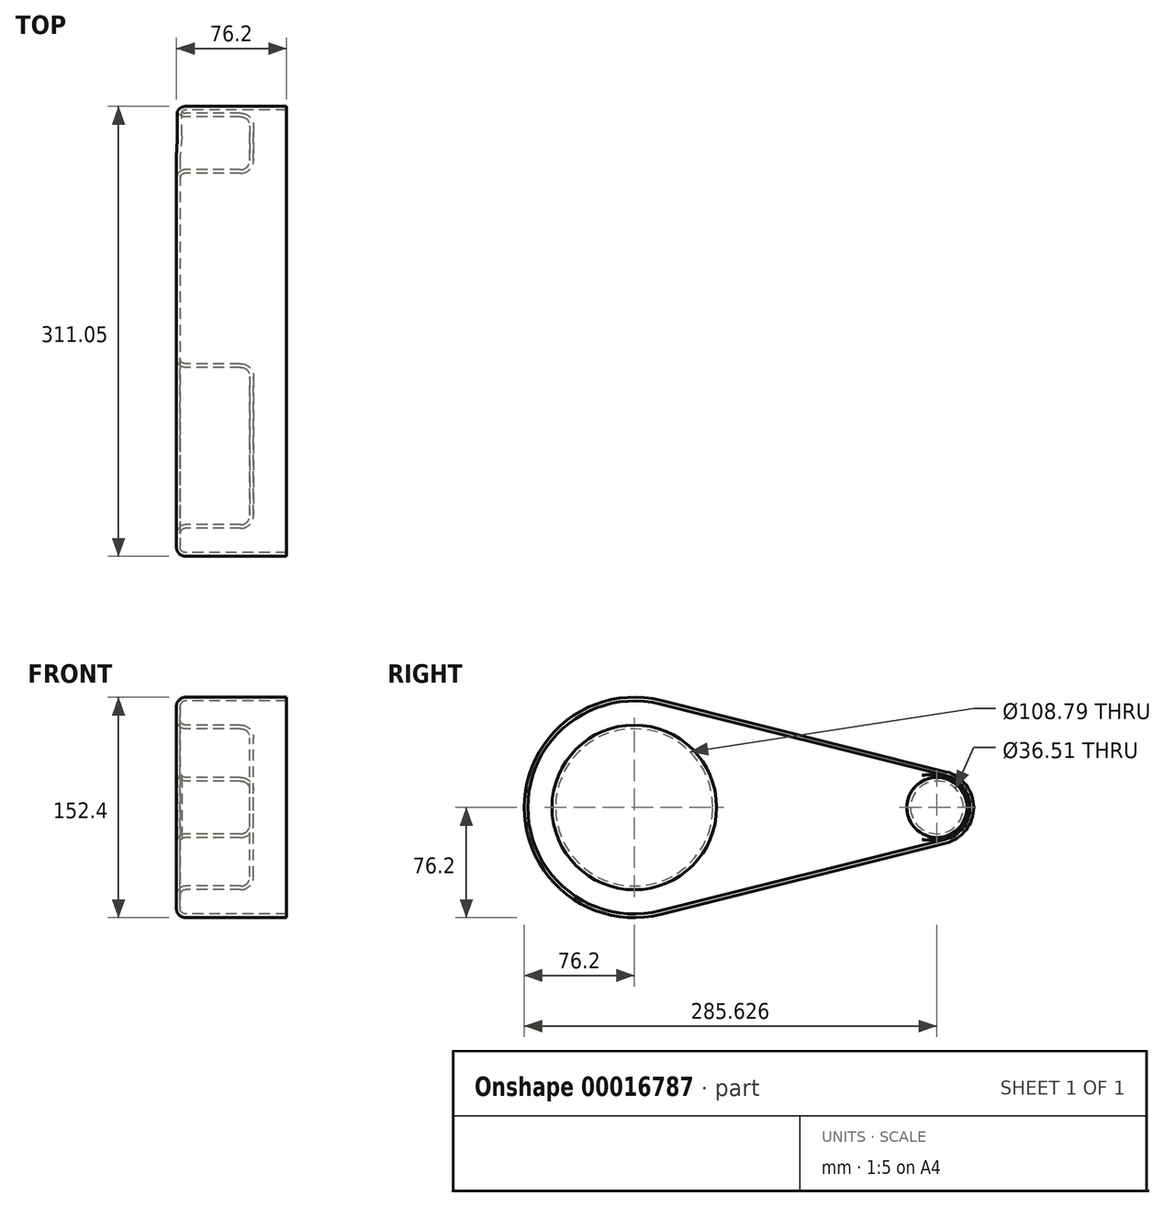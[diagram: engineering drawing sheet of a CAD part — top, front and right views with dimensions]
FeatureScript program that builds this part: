
annotation { "Feature Type Name" : "Feature", "Feature Type Description" : "" }
export const myFeature = defineFeature(function(context is Context, id is Id, definition is map)
    precondition{}
    {
        {
            var Q0;
            Q0=qCreatedBy(makeId("Right.planeOp"),FACE);
            var sketch = newSketch(context, id + "F0", { "sketchPlane" : qUnion([Q0])});
            skCircle(sketch, "E0", {"center": v(0, 0) * mm, "radius": 76.2 * mm});
            skCircle(sketch, "E1", {"center": v(209.45, 0) * mm, "radius": 25.4 * mm});
            skLineSegment(sketch, "E2", {"start": v(18.48, 73.92) * mm, "end": v(215.61, 24.64) * mm});
            skLineSegment(sketch, "E3", {"start": v(18.48, -73.92) * mm, "end": v(215.61, -24.64) * mm});
            skSolve(sketch);
        }
        {
            var Q0;
            {var subQ0=sQuery(id+"F0.wireOp",EDGE,"E0");var subQ2=makeQuery(id+"F0.imprint","INTERSECT",VERTEX,{"derivedFrom":[subQ0,sQuery(id+"F0.wireOp",EDGE,"E2")]});Q0=makeQuery(id+"F0.imprint","IMPRINT",FACE,{"disambiguationData":[TD([[makeQuery(id+"F0.imprint","IMPRINT",EDGE,{"disambiguationData":[TD([[subQ2,-1.0]])],"derivedFrom":subQ0}),1.0]])]});}
            var Q1;
            {var subQ1=sQuery(id+"F0.wireOp",EDGE,"E2");Q1=makeQuery(id+"F0.imprint","IMPRINT",FACE,{"disambiguationData":[TD([[makeQuery(id+"F0.imprint","IMPRINT",EDGE,{"derivedFrom":subQ1}),-1.0]])]});}
            var Q2;
            {var subQ0=sQuery(id+"F0.wireOp",EDGE,"E1");var subQ2=makeQuery(id+"F0.imprint","INTERSECT",VERTEX,{"derivedFrom":[subQ0,sQuery(id+"F0.wireOp",EDGE,"E2")]});Q2=makeQuery(id+"F0.imprint","IMPRINT",FACE,{"disambiguationData":[TD([[makeQuery(id+"F0.imprint","IMPRINT",EDGE,{"disambiguationData":[TD([[subQ2,-1.0]])],"derivedFrom":subQ0}),1.0]])]});}
            extrude(context, id + "F1", {"entities" : qUnion([Q0, Q1, Q2]), "depth" : 76.2 * mm});
        }
        {
            var Q0;
            {var subQ0=sQuery(id+"F0.wireOp",EDGE,"E0");var subQ2=makeQuery(id+"F0.imprint","INTERSECT",VERTEX,{"derivedFrom":[subQ0,sQuery(id+"F0.wireOp",EDGE,"E2")]});Q0=makeQuery(id+"F0.imprint","IMPRINT",FACE,{"disambiguationData":[TD([[makeQuery(id+"F0.imprint","IMPRINT",EDGE,{"disambiguationData":[TD([[subQ2,-1.0]])],"derivedFrom":subQ0}),1.0]])]});}
            var sketch = newSketch(context, id + "F2", { "sketchPlane" : qUnion([Q0])});
            skCircle(sketch, "E4", {"center": v(0, 0) * mm, "radius": 54.4 * mm});
            skCircle(sketch, "E5", {"center": v(209.43, 0) * mm, "radius": 18.25 * mm});
            skSolve(sketch);
        }
        {
            var Q0;
            Q0=makeQuery(id+"F2.imprint","IMPRINT",FACE,{"disambiguationData":[TD([[makeQuery(id+"F2.imprint","IMPRINT",EDGE,{"derivedFrom":sQuery(id+"F2.wireOp",EDGE,"E5")}),1.0]])]});
            var Q1;
            Q1=makeQuery(id+"F2.imprint","IMPRINT",FACE,{"disambiguationData":[TD([[makeQuery(id+"F2.imprint","IMPRINT",EDGE,{"derivedFrom":sQuery(id+"F2.wireOp",EDGE,"E4")}),1.0]])]});
            extrude(context, id + "F3", {"entities" : qUnion([Q0, Q1]), "operationType" : NewBodyOperationType.REMOVE, "depth" : 50.8 * mm});
        }
        {
            var Q0;
            Q0=makeQuery(id+"F1.opExtrude","CAP_FACE",FACE,{"disambiguationData":[OSD([sQuery(id+"F0.wireOp",EDGE,"E0"),sQuery(id+"F0.wireOp",EDGE,"E1"),sQuery(id+"F0.wireOp",EDGE,"E2"),sQuery(id+"F0.wireOp",EDGE,"E3")])],"isStart":true});
            var Q1;
            Q1=makeQuery(id+"F3.boolean.opBoolean","COPY",EDGE,{"derivedFrom":makeQuery(id+"F3.opExtrude","CAP_EDGE",EDGE,{"disambiguationData":[OSD([sQuery(id+"F2.wireOp",EDGE,"E4")])],"isStart":false})});
            var Q2;
            Q2=makeQuery(id+"F3.boolean.opBoolean","COPY",EDGE,{"derivedFrom":makeQuery(id+"F3.opExtrude","CAP_EDGE",EDGE,{"disambiguationData":[OSD([sQuery(id+"F2.wireOp",EDGE,"E5")])],"isStart":false})});
            fillet(context, id + "F4", {"entities" : qUnion([Q0, Q1, Q2]), "radius" : 6.35 * mm, "tangentPropagation" : true, "allowEdgeOverflow" : false});
        }
        {
            var Q0;
            Q0=makeQuery(id+"F1.opExtrude","CAP_FACE",FACE,{"disambiguationData":[OSD([sQuery(id+"F0.wireOp",EDGE,"E0"),sQuery(id+"F0.wireOp",EDGE,"E1"),sQuery(id+"F0.wireOp",EDGE,"E2"),sQuery(id+"F0.wireOp",EDGE,"E3")])],"isStart":false});
            shell(context, id + "F5", {"entities" : qUnion([Q0]), "thickness" : 2.54 * mm});
        }
    });
